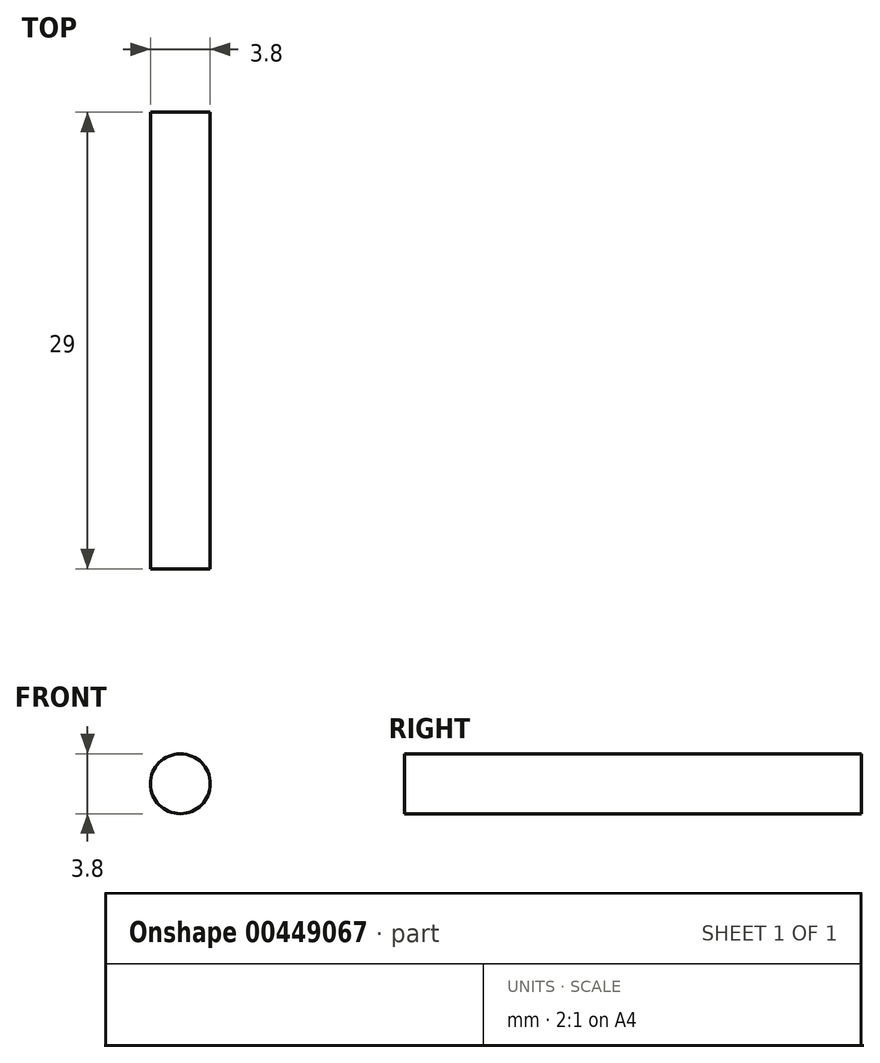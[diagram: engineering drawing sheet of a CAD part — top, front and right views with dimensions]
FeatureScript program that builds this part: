
annotation { "Feature Type Name" : "Feature", "Feature Type Description" : "" }
export const myFeature = defineFeature(function(context is Context, id is Id, definition is map)
    precondition{}
    {
        {
            var Q0;
            Q0=qCreatedBy(makeId("Front.planeOp"),FACE);
            var sketch = newSketch(context, id + "F0", { "sketchPlane" : qUnion([Q0])});
            skCircle(sketch, "E0", {"center": v(0, 0) * mm, "radius": 1.9 * mm});
            skSolve(sketch);
        }
        {
            var Q0;
            Q0=makeQuery(id+"F0.imprint","IMPRINT",FACE,{"disambiguationData":[TD([[makeQuery(id+"F0.imprint","IMPRINT",EDGE,{"derivedFrom":sQuery(id+"F0.wireOp",EDGE,"E0")}),1.0]])]});
            extrude(context, id + "F1", {"entities" : qUnion([Q0]), "depth" : (5 * 5 + 4 * 1) * mm});
        }
    });
